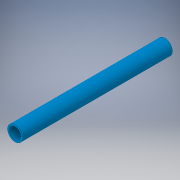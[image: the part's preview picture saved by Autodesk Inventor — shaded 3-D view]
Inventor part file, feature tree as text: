
AUTODESK INVENTOR PART (.ipt)
format: ipt  version: 2018.2 (Build 222227000, 227)  size: 106,496 bytes
history: native  units: in
note: dims shown in document units (in); Inventor stores cm internally (conversion verified against a paired STEP export)
features: extrude x1, sketch x1
ambient origin geometry x8: Origin, YZ Plane, XZ Plane, XY Plane, X Axis, Y Axis, Z Axis, Center Point
bodies: Solid1 (feature_tree)
feature tree (2):
  extrude  "Extrusion1"  Depth=13.0in
  sketch  "Sketch1"  dims[d0=1.315in d1=1.0in d2=13.0in d3=0.0in]
